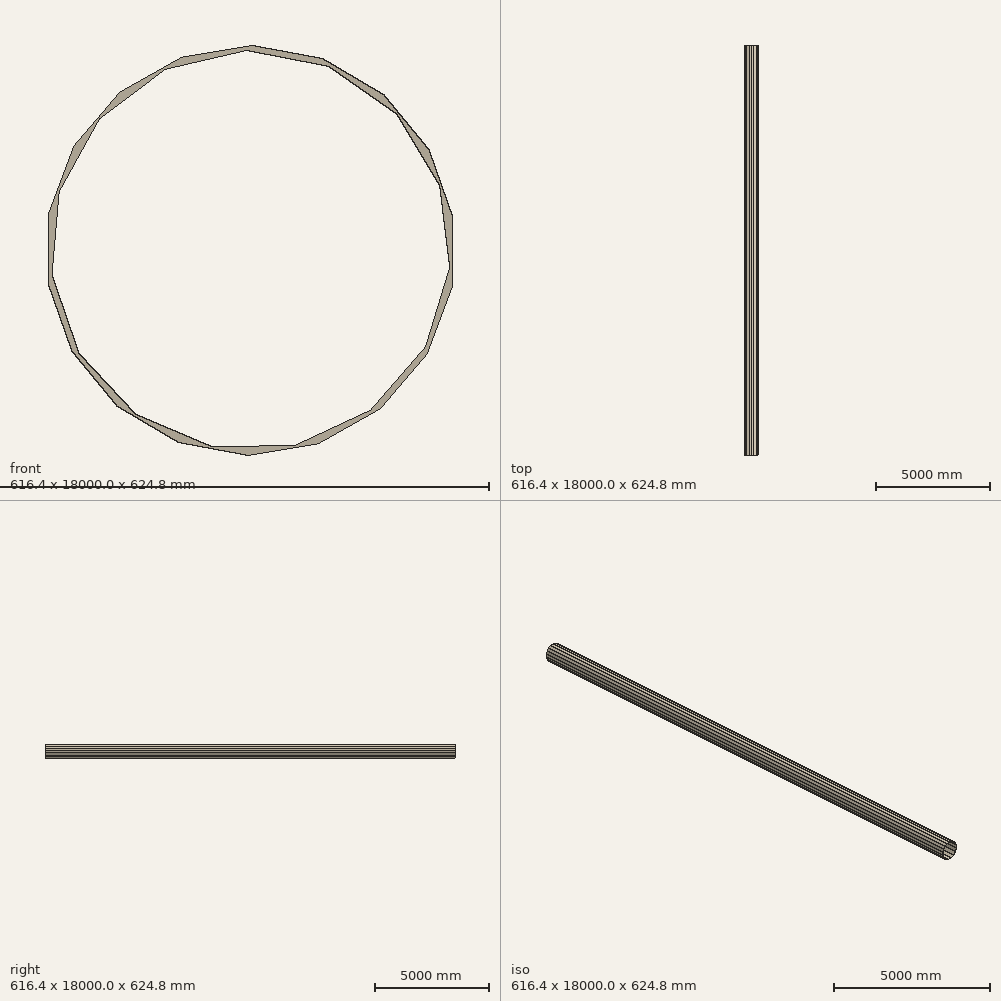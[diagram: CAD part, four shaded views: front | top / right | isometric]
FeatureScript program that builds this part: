
annotation { "Feature Type Name" : "Feature", "Feature Type Description" : "" }
export const myFeature = defineFeature(function(context is Context, id is Id, definition is map)
    precondition{}
    {
        {
            var Q0;
            Q0=qCreatedBy(makeId("Front.planeOp"),FACE);
            var sketch = newSketch(context, id + "F0", { "sketchPlane" : qUnion([Q0])});
            skCircle(sketch, "E0.cCircle", {"center": v(0, 0) * mm, "radius": 312.42 * mm, "construction": true});
            skLineSegment(sketch, "E0.0", {"start": v(104.01, -294.6) * mm, "end": v(-3.02, -312.4) * mm});
            skLineSegment(sketch, "E0.1", {"start": v(-3.02, -312.4) * mm, "end": v(-109.68, -292.53) * mm});
            skLineSegment(sketch, "E0.2", {"start": v(-109.68, -292.53) * mm, "end": v(-203.12, -237.38) * mm});
            skLineSegment(sketch, "E0.3", {"start": v(-203.12, -237.38) * mm, "end": v(-272.06, -153.6) * mm});
            skLineSegment(sketch, "E0.4", {"start": v(-272.06, -153.6) * mm, "end": v(-308.18, -51.28) * mm});
            skLineSegment(sketch, "E0.5", {"start": v(-308.18, -51.28) * mm, "end": v(-307.14, 57.22) * mm});
            skLineSegment(sketch, "E0.6", {"start": v(-307.14, 57.22) * mm, "end": v(-269.04, 158.81) * mm});
            skLineSegment(sketch, "E0.7", {"start": v(-269.04, 158.81) * mm, "end": v(-198.5, 241.26) * mm});
            skLineSegment(sketch, "E0.8", {"start": v(-198.5, 241.26) * mm, "end": v(-104.01, 294.6) * mm});
            skLineSegment(sketch, "E0.9", {"start": v(-104.01, 294.6) * mm, "end": v(3.02, 312.4) * mm});
            skLineSegment(sketch, "E0.10", {"start": v(3.02, 312.4) * mm, "end": v(109.68, 292.53) * mm});
            skLineSegment(sketch, "E0.11", {"start": v(109.68, 292.53) * mm, "end": v(203.12, 237.38) * mm});
            skLineSegment(sketch, "E0.12", {"start": v(203.12, 237.38) * mm, "end": v(272.06, 153.6) * mm});
            skLineSegment(sketch, "E0.13", {"start": v(272.06, 153.6) * mm, "end": v(308.18, 51.28) * mm});
            skLineSegment(sketch, "E0.14", {"start": v(308.18, 51.28) * mm, "end": v(307.14, -57.22) * mm});
            skLineSegment(sketch, "E0.15", {"start": v(307.14, -57.22) * mm, "end": v(269.04, -158.81) * mm});
            skLineSegment(sketch, "E0.16", {"start": v(269.04, -158.81) * mm, "end": v(198.5, -241.26) * mm});
            skLineSegment(sketch, "E0.17", {"start": v(198.5, -241.26) * mm, "end": v(104.01, -294.6) * mm});
            skCircle(sketch, "E1.cCircle", {"center": v(0, 0) * mm, "radius": 304.8 * mm, "construction": true});
            skLineSegment(sketch, "E1.0", {"start": v(183.54, -243.34) * mm, "end": v(68.7, -296.96) * mm});
            skLineSegment(sketch, "E1.1", {"start": v(68.7, -296.96) * mm, "end": v(-58.02, -299.23) * mm});
            skLineSegment(sketch, "E1.2", {"start": v(-58.02, -299.23) * mm, "end": v(-174.71, -249.76) * mm});
            skLineSegment(sketch, "E1.3", {"start": v(-174.71, -249.76) * mm, "end": v(-261.2, -157.1) * mm});
            skLineSegment(sketch, "E1.4", {"start": v(-261.2, -157.1) * mm, "end": v(-302.51, -37.28) * mm});
            skLineSegment(sketch, "E1.5", {"start": v(-302.51, -37.28) * mm, "end": v(-291.52, 88.98) * mm});
            skLineSegment(sketch, "E1.6", {"start": v(-291.52, 88.98) * mm, "end": v(-230.13, 199.86) * mm});
            skLineSegment(sketch, "E1.7", {"start": v(-230.13, 199.86) * mm, "end": v(-128.94, 276.18) * mm});
            skLineSegment(sketch, "E1.8", {"start": v(-128.94, 276.18) * mm, "end": v(-5.46, 304.75) * mm});
            skLineSegment(sketch, "E1.9", {"start": v(-5.46, 304.75) * mm, "end": v(118.97, 280.62) * mm});
            skLineSegment(sketch, "E1.10", {"start": v(118.97, 280.62) * mm, "end": v(222.82, 207.97) * mm});
            skLineSegment(sketch, "E1.11", {"start": v(222.82, 207.97) * mm, "end": v(288.15, 99.36) * mm});
            skLineSegment(sketch, "E1.12", {"start": v(288.15, 99.36) * mm, "end": v(303.65, -26.43) * mm});
            skLineSegment(sketch, "E1.13", {"start": v(303.65, -26.43) * mm, "end": v(266.65, -147.65) * mm});
            skLineSegment(sketch, "E1.14", {"start": v(266.65, -147.65) * mm, "end": v(183.54, -243.34) * mm});
            skSolve(sketch);
        }
        {
            var Q0;
            Q0=makeQuery(id+"F0.imprint","IMPRINT",FACE,{"disambiguationData":[TD([[makeQuery(id+"F0.imprint","IMPRINT",EDGE,{"derivedFrom":sQuery(id+"F0.wireOp",EDGE,"E0.0")}),-1.0]])]});
            extrude(context, id + "F1", {"entities" : qUnion([Q0]), "depth" : 18000 * mm});
        }
    });
